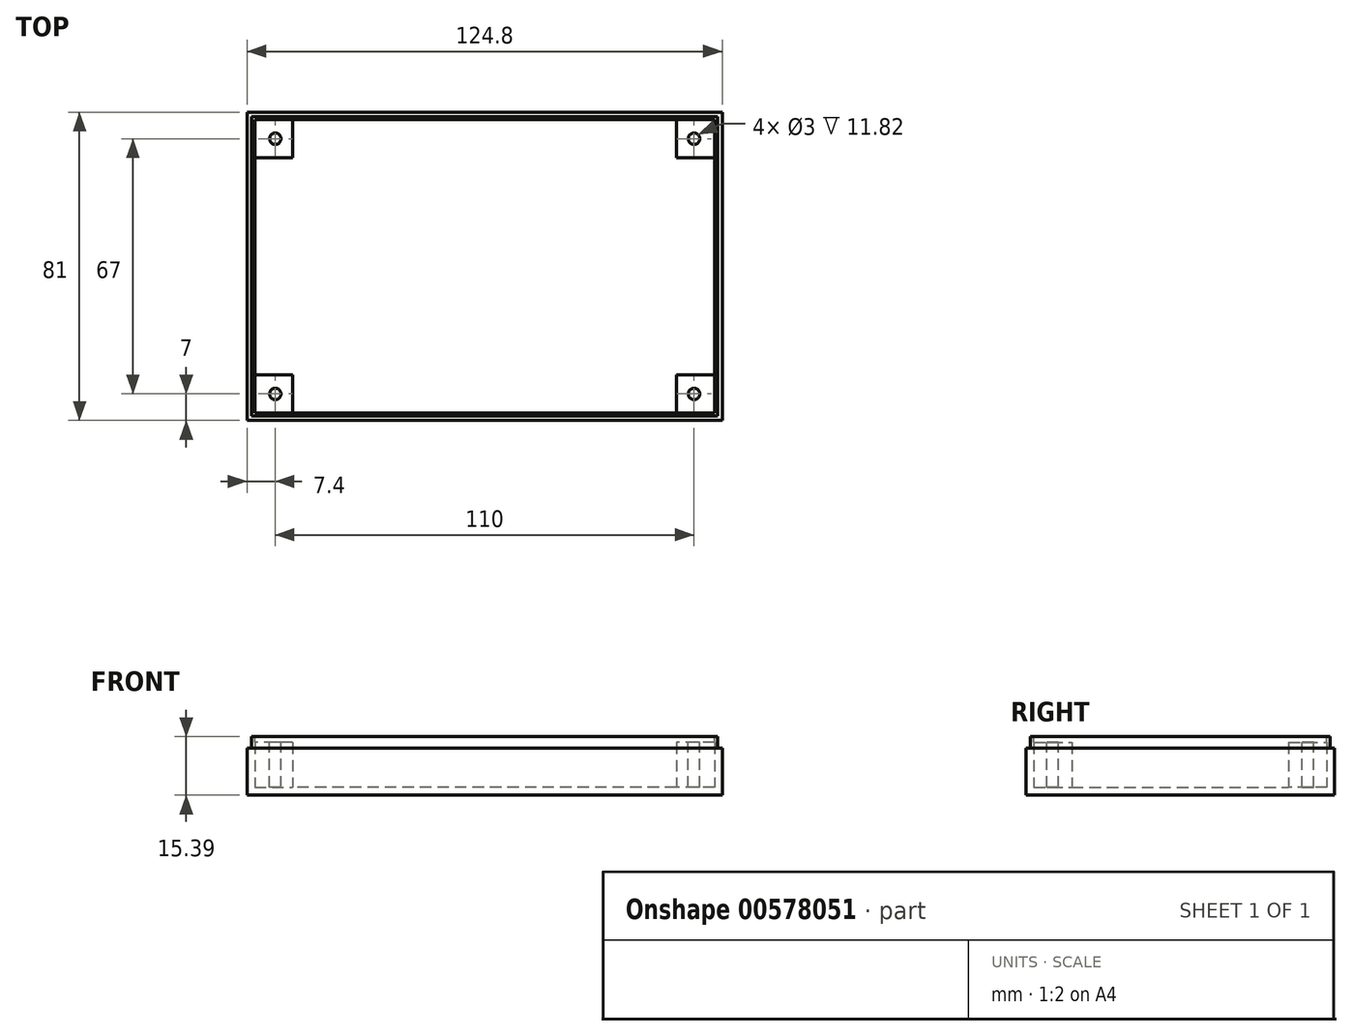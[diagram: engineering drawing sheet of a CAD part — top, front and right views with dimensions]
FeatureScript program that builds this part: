
annotation { "Feature Type Name" : "Feature", "Feature Type Description" : "" }
export const myFeature = defineFeature(function(context is Context, id is Id, definition is map)
    precondition{}
    {
        {
            var Q0;
            Q0=qCreatedBy(makeId("Top.planeOp"),FACE);
            var sketch = newSketch(context, id + "F0", { "sketchPlane" : qUnion([Q0])});
            skLineSegment(sketch, "E0.bottom", {"start": v(-62.4, -40.5) * mm, "end": v(62.4, -40.5) * mm});
            skLineSegment(sketch, "E0.top", {"start": v(-62.4, 40.5) * mm, "end": v(62.4, 40.5) * mm});
            skLineSegment(sketch, "E0.left", {"start": v(-62.4, -40.5) * mm, "end": v(-62.4, 40.5) * mm});
            skLineSegment(sketch, "E0.right", {"start": v(62.4, -40.5) * mm, "end": v(62.4, 40.5) * mm});
            skPoint(sketch, "E0.middle", {"position": v(0, 0) * mm});
            skSolve(sketch);
        }
        {
            var Q0;
            Q0=makeQuery(id+"F0.imprint","IMPRINT",FACE,{"disambiguationData":[TD([[makeQuery(id+"F0.imprint","IMPRINT",EDGE,{"derivedFrom":sQuery(id+"F0.wireOp",EDGE,"E0.bottom")}),1.0]])]});
            extrude(context, id + "F1", {"entities" : qUnion([Q0]), "depth" : 15.4 * mm, "offsetDistance" : 25 * mm});
        }
        {
            var Q0;
            Q0=makeQuery(id+"F1.opExtrude","CAP_FACE",FACE,{"disambiguationData":[OSD([sQuery(id+"F0.wireOp",EDGE,"E0.bottom"),sQuery(id+"F0.wireOp",EDGE,"E0.top"),sQuery(id+"F0.wireOp",EDGE,"E0.left"),sQuery(id+"F0.wireOp",EDGE,"E0.right")])],"isStart":false});
            var sketch = newSketch(context, id + "F2", { "sketchPlane" : qUnion([Q0])});
            skLineSegment(sketch, "E1.bottom", {"start": v(60.4, -38.5) * mm, "end": v(-60.4, -38.5) * mm});
            skLineSegment(sketch, "E1.top", {"start": v(60.4, 38.5) * mm, "end": v(-60.4, 38.5) * mm});
            skLineSegment(sketch, "E1.left", {"start": v(60.4, -38.5) * mm, "end": v(60.4, 38.5) * mm});
            skLineSegment(sketch, "E1.right", {"start": v(-60.4, -38.5) * mm, "end": v(-60.4, 38.5) * mm});
            skPoint(sketch, "E1.middle", {"position": v(0, 0) * mm});
            skSolve(sketch);
        }
        {
            var Q0;
            Q0=makeQuery(id+"F2.imprint","IMPRINT",FACE,{"disambiguationData":[TD([[makeQuery(id+"F2.imprint","IMPRINT",EDGE,{"derivedFrom":sQuery(id+"F2.wireOp",EDGE,"E1.bottom")}),-1.0]])]});
            extrude(context, id + "F3", {"entities" : qUnion([Q0]), "operationType" : NewBodyOperationType.REMOVE, "oppositeDirection" : true, "depth" : 13.4 * mm, "offsetDistance" : 25 * mm});
        }
        {
            var Q0;
            Q0=makeQuery(id+"F1.opExtrude","SWEPT_FACE",FACE,{"disambiguationData":[OSD([sQuery(id+"F0.wireOp",EDGE,"E0.top")])]});
            var sketch = newSketch(context, id + "F4", { "sketchPlane" : qUnion([Q0])});
            skLineSegment(sketch, "E2.bottom", {"start": v(-62.4, 15.4) * mm, "end": v(62.4, 15.4) * mm});
            skLineSegment(sketch, "E2.top", {"start": v(-62.4, 12.4) * mm, "end": v(62.4, 12.4) * mm});
            skLineSegment(sketch, "E2.left", {"start": v(-62.4, 15.4) * mm, "end": v(-62.4, 12.4) * mm});
            skLineSegment(sketch, "E2.right", {"start": v(62.4, 15.4) * mm, "end": v(62.4, 12.4) * mm});
            skSolve(sketch);
        }
        {
            var Q0;
            Q0=makeQuery(id+"F4.imprint","IMPRINT",FACE,{"disambiguationData":[TD([[makeQuery(id+"F4.imprint","IMPRINT",EDGE,{"derivedFrom":sQuery(id+"F4.wireOp",EDGE,"E2.bottom")}),1.0]])]});
            extrude(context, id + "F5", {"entities" : qUnion([Q0]), "operationType" : NewBodyOperationType.REMOVE, "oppositeDirection" : true, "depth" : 1.15 * mm, "offsetDistance" : 25 * mm});
        }
        {
            var Q0;
            Q0=makeQuery(id+"F1.opExtrude","SWEPT_FACE",FACE,{"disambiguationData":[OSD([sQuery(id+"F0.wireOp",EDGE,"E0.bottom")])]});
            var sketch = newSketch(context, id + "F6", { "sketchPlane" : qUnion([Q0])});
            skLineSegment(sketch, "E3.bottom", {"start": v(-62.4, 15.4) * mm, "end": v(62.4, 15.4) * mm});
            skLineSegment(sketch, "E3.top", {"start": v(-62.4, 12.4) * mm, "end": v(62.4, 12.4) * mm});
            skLineSegment(sketch, "E3.left", {"start": v(-62.4, 15.4) * mm, "end": v(-62.4, 12.4) * mm});
            skLineSegment(sketch, "E3.right", {"start": v(62.4, 15.4) * mm, "end": v(62.4, 12.4) * mm});
            skSolve(sketch);
        }
        {
            var Q0;
            Q0=makeQuery(id+"F6.imprint","IMPRINT",FACE,{"disambiguationData":[TD([[makeQuery(id+"F6.imprint","IMPRINT",EDGE,{"derivedFrom":sQuery(id+"F6.wireOp",EDGE,"E3.bottom")}),-1.0]])]});
            extrude(context, id + "F7", {"entities" : qUnion([Q0]), "operationType" : NewBodyOperationType.REMOVE, "oppositeDirection" : true, "depth" : 1.15 * mm, "offsetDistance" : 25 * mm});
        }
        {
            var Q0;
            Q0=makeQuery(id+"F1.opExtrude","SWEPT_FACE",FACE,{"disambiguationData":[OSD([sQuery(id+"F0.wireOp",EDGE,"E0.right")])]});
            var sketch = newSketch(context, id + "F8", { "sketchPlane" : qUnion([Q0])});
            skLineSegment(sketch, "E4.bottom", {"start": v(-39.35, 15.4) * mm, "end": v(39.35, 15.4) * mm});
            skLineSegment(sketch, "E4.top", {"start": v(-39.35, 12.4) * mm, "end": v(39.35, 12.4) * mm});
            skLineSegment(sketch, "E4.left", {"start": v(-39.35, 15.4) * mm, "end": v(-39.35, 12.4) * mm});
            skLineSegment(sketch, "E4.right", {"start": v(39.35, 15.4) * mm, "end": v(39.35, 12.4) * mm});
            skSolve(sketch);
        }
        {
            var Q0;
            Q0=makeQuery(id+"F8.imprint","IMPRINT",FACE,{"disambiguationData":[TD([[makeQuery(id+"F8.imprint","IMPRINT",EDGE,{"derivedFrom":sQuery(id+"F8.wireOp",EDGE,"E4.bottom")}),-1.0]])]});
            extrude(context, id + "F9", {"entities" : qUnion([Q0]), "operationType" : NewBodyOperationType.REMOVE, "oppositeDirection" : true, "depth" : 1.15 * mm, "offsetDistance" : 25 * mm});
        }
        {
            var Q0;
            Q0=makeQuery(id+"F1.opExtrude","SWEPT_FACE",FACE,{"disambiguationData":[OSD([sQuery(id+"F0.wireOp",EDGE,"E0.left")])]});
            var sketch = newSketch(context, id + "F10", { "sketchPlane" : qUnion([Q0])});
            skLineSegment(sketch, "E5.bottom", {"start": v(-39.35, 15.4) * mm, "end": v(39.35, 15.4) * mm});
            skLineSegment(sketch, "E5.top", {"start": v(-39.35, 12.4) * mm, "end": v(39.35, 12.4) * mm});
            skLineSegment(sketch, "E5.left", {"start": v(-39.35, 15.4) * mm, "end": v(-39.35, 12.4) * mm});
            skLineSegment(sketch, "E5.right", {"start": v(39.35, 15.4) * mm, "end": v(39.35, 12.4) * mm});
            skSolve(sketch);
        }
        {
            var Q0;
            Q0=makeQuery(id+"F10.imprint","IMPRINT",FACE,{"disambiguationData":[TD([[makeQuery(id+"F10.imprint","IMPRINT",EDGE,{"derivedFrom":sQuery(id+"F10.wireOp",EDGE,"E5.bottom")}),1.0]])]});
            extrude(context, id + "F11", {"entities" : qUnion([Q0]), "operationType" : NewBodyOperationType.REMOVE, "oppositeDirection" : true, "depth" : 1.15 * mm, "offsetDistance" : 25 * mm});
        }
        {
            var Q0;
            Q0=makeQuery(id+"F3.boolean.opBoolean","COPY",FACE,{"derivedFrom":makeQuery(id+"F3.opExtrude","CAP_FACE",FACE,{"disambiguationData":[OSD([sQuery(id+"F2.wireOp",EDGE,"E1.bottom"),sQuery(id+"F2.wireOp",EDGE,"E1.top"),sQuery(id+"F2.wireOp",EDGE,"E1.left"),sQuery(id+"F2.wireOp",EDGE,"E1.right")])],"isStart":false})});
            var sketch = newSketch(context, id + "F12", { "sketchPlane" : qUnion([Q0])});
            skLineSegment(sketch, "E6.bottom", {"start": v(-60.4, 38.5) * mm, "end": v(-50.4, 38.5) * mm});
            skLineSegment(sketch, "E6.top", {"start": v(-60.4, 28.5) * mm, "end": v(-50.4, 28.5) * mm});
            skLineSegment(sketch, "E6.left", {"start": v(-60.4, 38.5) * mm, "end": v(-60.4, 28.5) * mm});
            skLineSegment(sketch, "E6.right", {"start": v(-50.4, 38.5) * mm, "end": v(-50.4, 28.5) * mm});
            skSolve(sketch);
        }
        {
            var Q0;
            Q0=makeQuery(id+"F12.imprint","IMPRINT",FACE,{"disambiguationData":[TD([[makeQuery(id+"F12.imprint","IMPRINT",EDGE,{"derivedFrom":sQuery(id+"F12.wireOp",EDGE,"E6.bottom")}),1.0]])]});
            extrude(context, id + "F13", {"entities" : qUnion([Q0]), "operationType" : NewBodyOperationType.ADD, "depth" : 11.82 * mm, "offsetDistance" : 25 * mm});
        }
        {
            var Q0;
            Q0=makeQuery(id+"F3.boolean.opBoolean","COPY",FACE,{"derivedFrom":makeQuery(id+"F3.opExtrude","CAP_FACE",FACE,{"disambiguationData":[OSD([sQuery(id+"F2.wireOp",EDGE,"E1.bottom"),sQuery(id+"F2.wireOp",EDGE,"E1.top"),sQuery(id+"F2.wireOp",EDGE,"E1.left"),sQuery(id+"F2.wireOp",EDGE,"E1.right")])],"isStart":false})});
            var sketch = newSketch(context, id + "F14", { "sketchPlane" : qUnion([Q0])});
            skLineSegment(sketch, "E7.bottom", {"start": v(-60.4, -38.5) * mm, "end": v(-50.4, -38.5) * mm});
            skLineSegment(sketch, "E7.top", {"start": v(-60.4, -28.5) * mm, "end": v(-50.4, -28.5) * mm});
            skLineSegment(sketch, "E7.left", {"start": v(-60.4, -38.5) * mm, "end": v(-60.4, -28.5) * mm});
            skLineSegment(sketch, "E7.right", {"start": v(-50.4, -38.5) * mm, "end": v(-50.4, -28.5) * mm});
            skSolve(sketch);
        }
        {
            var Q0;
            Q0=makeQuery(id+"F14.imprint","IMPRINT",FACE,{"disambiguationData":[TD([[makeQuery(id+"F14.imprint","IMPRINT",EDGE,{"derivedFrom":sQuery(id+"F14.wireOp",EDGE,"E7.bottom")}),-1.0]])]});
            extrude(context, id + "F15", {"entities" : qUnion([Q0]), "operationType" : NewBodyOperationType.ADD, "depth" : 11.82 * mm, "offsetDistance" : 25 * mm});
        }
        {
            var Q0;
            Q0=makeQuery(id+"F3.boolean.opBoolean","COPY",FACE,{"derivedFrom":makeQuery(id+"F3.opExtrude","CAP_FACE",FACE,{"disambiguationData":[OSD([sQuery(id+"F2.wireOp",EDGE,"E1.bottom"),sQuery(id+"F2.wireOp",EDGE,"E1.top"),sQuery(id+"F2.wireOp",EDGE,"E1.left"),sQuery(id+"F2.wireOp",EDGE,"E1.right")])],"isStart":false})});
            var sketch = newSketch(context, id + "F16", { "sketchPlane" : qUnion([Q0])});
            skLineSegment(sketch, "E8.bottom", {"start": v(60.4, -38.5) * mm, "end": v(50.4, -38.5) * mm});
            skLineSegment(sketch, "E8.top", {"start": v(60.4, -28.5) * mm, "end": v(50.4, -28.5) * mm});
            skLineSegment(sketch, "E8.left", {"start": v(60.4, -38.5) * mm, "end": v(60.4, -28.5) * mm});
            skLineSegment(sketch, "E8.right", {"start": v(50.4, -38.5) * mm, "end": v(50.4, -28.5) * mm});
            skSolve(sketch);
        }
        {
            var Q0;
            Q0=makeQuery(id+"F16.imprint","IMPRINT",FACE,{"disambiguationData":[TD([[makeQuery(id+"F16.imprint","IMPRINT",EDGE,{"derivedFrom":sQuery(id+"F16.wireOp",EDGE,"E8.bottom")}),-1.0]])]});
            extrude(context, id + "F17", {"entities" : qUnion([Q0]), "operationType" : NewBodyOperationType.ADD, "depth" : 11.82 * mm, "offsetDistance" : 25 * mm});
        }
        {
            var Q0;
            Q0=makeQuery(id+"F3.boolean.opBoolean","COPY",FACE,{"derivedFrom":makeQuery(id+"F3.opExtrude","CAP_FACE",FACE,{"disambiguationData":[OSD([sQuery(id+"F2.wireOp",EDGE,"E1.bottom"),sQuery(id+"F2.wireOp",EDGE,"E1.top"),sQuery(id+"F2.wireOp",EDGE,"E1.left"),sQuery(id+"F2.wireOp",EDGE,"E1.right")])],"isStart":false})});
            var sketch = newSketch(context, id + "F18", { "sketchPlane" : qUnion([Q0])});
            skLineSegment(sketch, "E9.bottom", {"start": v(60.4, 38.5) * mm, "end": v(50.4, 38.5) * mm});
            skLineSegment(sketch, "E9.top", {"start": v(60.4, 28.5) * mm, "end": v(50.4, 28.5) * mm});
            skLineSegment(sketch, "E9.left", {"start": v(60.4, 38.5) * mm, "end": v(60.4, 28.5) * mm});
            skLineSegment(sketch, "E9.right", {"start": v(50.4, 38.5) * mm, "end": v(50.4, 28.5) * mm});
            skSolve(sketch);
        }
        {
            var Q0;
            Q0=makeQuery(id+"F18.imprint","IMPRINT",FACE,{"disambiguationData":[TD([[makeQuery(id+"F18.imprint","IMPRINT",EDGE,{"derivedFrom":sQuery(id+"F18.wireOp",EDGE,"E9.bottom")}),1.0]])]});
            extrude(context, id + "F19", {"entities" : qUnion([Q0]), "operationType" : NewBodyOperationType.ADD, "depth" : 11.82 * mm, "offsetDistance" : 25 * mm});
        }
        {
            var Q0;
            Q0=makeQuery(id+"F13.opExtrude","CAP_FACE",FACE,{"disambiguationData":[OSD([sQuery(id+"F12.wireOp",EDGE,"E6.bottom"),sQuery(id+"F12.wireOp",EDGE,"E6.top"),sQuery(id+"F12.wireOp",EDGE,"E6.left"),sQuery(id+"F12.wireOp",EDGE,"E6.right")])],"isStart":false});
            var sketch = newSketch(context, id + "F20", { "sketchPlane" : qUnion([Q0])});
            skCircle(sketch, "E10", {"center": v(-55, 33.5) * mm, "radius": 1.5 * mm});
            skSolve(sketch);
        }
        {
            var Q0;
            Q0=makeQuery(id+"F20.imprint","IMPRINT",FACE,{"disambiguationData":[TD([[makeQuery(id+"F20.imprint","IMPRINT",EDGE,{"derivedFrom":sQuery(id+"F20.wireOp",EDGE,"E10")}),1.0]])]});
            var Q1;
            Q1 = qSketchRegion(id + "F20", true);
            extrude(context, id + "F21", {"entities" : qUnion([Q0, Q1]), "operationType" : NewBodyOperationType.REMOVE, "oppositeDirection" : true, "depth" : 11.82 * mm, "offsetDistance" : 25 * mm});
        }
        {
            var Q0;
            Q0=makeQuery(id+"F15.opExtrude","CAP_FACE",FACE,{"disambiguationData":[OSD([sQuery(id+"F14.wireOp",EDGE,"E7.bottom"),sQuery(id+"F14.wireOp",EDGE,"E7.top"),sQuery(id+"F14.wireOp",EDGE,"E7.left"),sQuery(id+"F14.wireOp",EDGE,"E7.right")])],"isStart":false});
            var sketch = newSketch(context, id + "F22", { "sketchPlane" : qUnion([Q0])});
            skCircle(sketch, "E11", {"center": v(-55, -33.5) * mm, "radius": 1.5 * mm});
            skSolve(sketch);
        }
        {
            var Q0;
            Q0=makeQuery(id+"F22.imprint","IMPRINT",FACE,{"disambiguationData":[TD([[makeQuery(id+"F22.imprint","IMPRINT",EDGE,{"derivedFrom":sQuery(id+"F22.wireOp",EDGE,"E11")}),1.0]])]});
            extrude(context, id + "F23", {"entities" : qUnion([Q0]), "operationType" : NewBodyOperationType.REMOVE, "oppositeDirection" : true, "depth" : 11.82 * mm, "offsetDistance" : 25 * mm});
        }
        {
            var Q0;
            Q0=makeQuery(id+"F17.opExtrude","CAP_FACE",FACE,{"disambiguationData":[OSD([sQuery(id+"F16.wireOp",EDGE,"E8.bottom"),sQuery(id+"F16.wireOp",EDGE,"E8.top"),sQuery(id+"F16.wireOp",EDGE,"E8.left"),sQuery(id+"F16.wireOp",EDGE,"E8.right")])],"isStart":false});
            var sketch = newSketch(context, id + "F24", { "sketchPlane" : qUnion([Q0])});
            skCircle(sketch, "E12", {"center": v(55, -33.5) * mm, "radius": 1.5 * mm});
            skSolve(sketch);
        }
        {
            var Q0;
            Q0=makeQuery(id+"F24.imprint","IMPRINT",FACE,{"disambiguationData":[TD([[makeQuery(id+"F24.imprint","IMPRINT",EDGE,{"derivedFrom":sQuery(id+"F24.wireOp",EDGE,"E12")}),1.0]])]});
            extrude(context, id + "F25", {"entities" : qUnion([Q0]), "operationType" : NewBodyOperationType.REMOVE, "oppositeDirection" : true, "depth" : 11.82 * mm, "offsetDistance" : 25 * mm});
        }
        {
            var Q0;
            Q0=makeQuery(id+"F19.opExtrude","CAP_FACE",FACE,{"disambiguationData":[OSD([sQuery(id+"F18.wireOp",EDGE,"E9.bottom"),sQuery(id+"F18.wireOp",EDGE,"E9.top"),sQuery(id+"F18.wireOp",EDGE,"E9.left"),sQuery(id+"F18.wireOp",EDGE,"E9.right")])],"isStart":false});
            var sketch = newSketch(context, id + "F26", { "sketchPlane" : qUnion([Q0])});
            skCircle(sketch, "E13", {"center": v(55, 33.5) * mm, "radius": 1.5 * mm});
            skSolve(sketch);
        }
        {
            var Q0;
            Q0=makeQuery(id+"F26.imprint","IMPRINT",FACE,{"disambiguationData":[TD([[makeQuery(id+"F26.imprint","IMPRINT",EDGE,{"derivedFrom":sQuery(id+"F26.wireOp",EDGE,"E13")}),1.0]])]});
            extrude(context, id + "F27", {"entities" : qUnion([Q0]), "operationType" : NewBodyOperationType.REMOVE, "oppositeDirection" : true, "depth" : 11.82 * mm, "offsetDistance" : 25 * mm});
        }
    });
